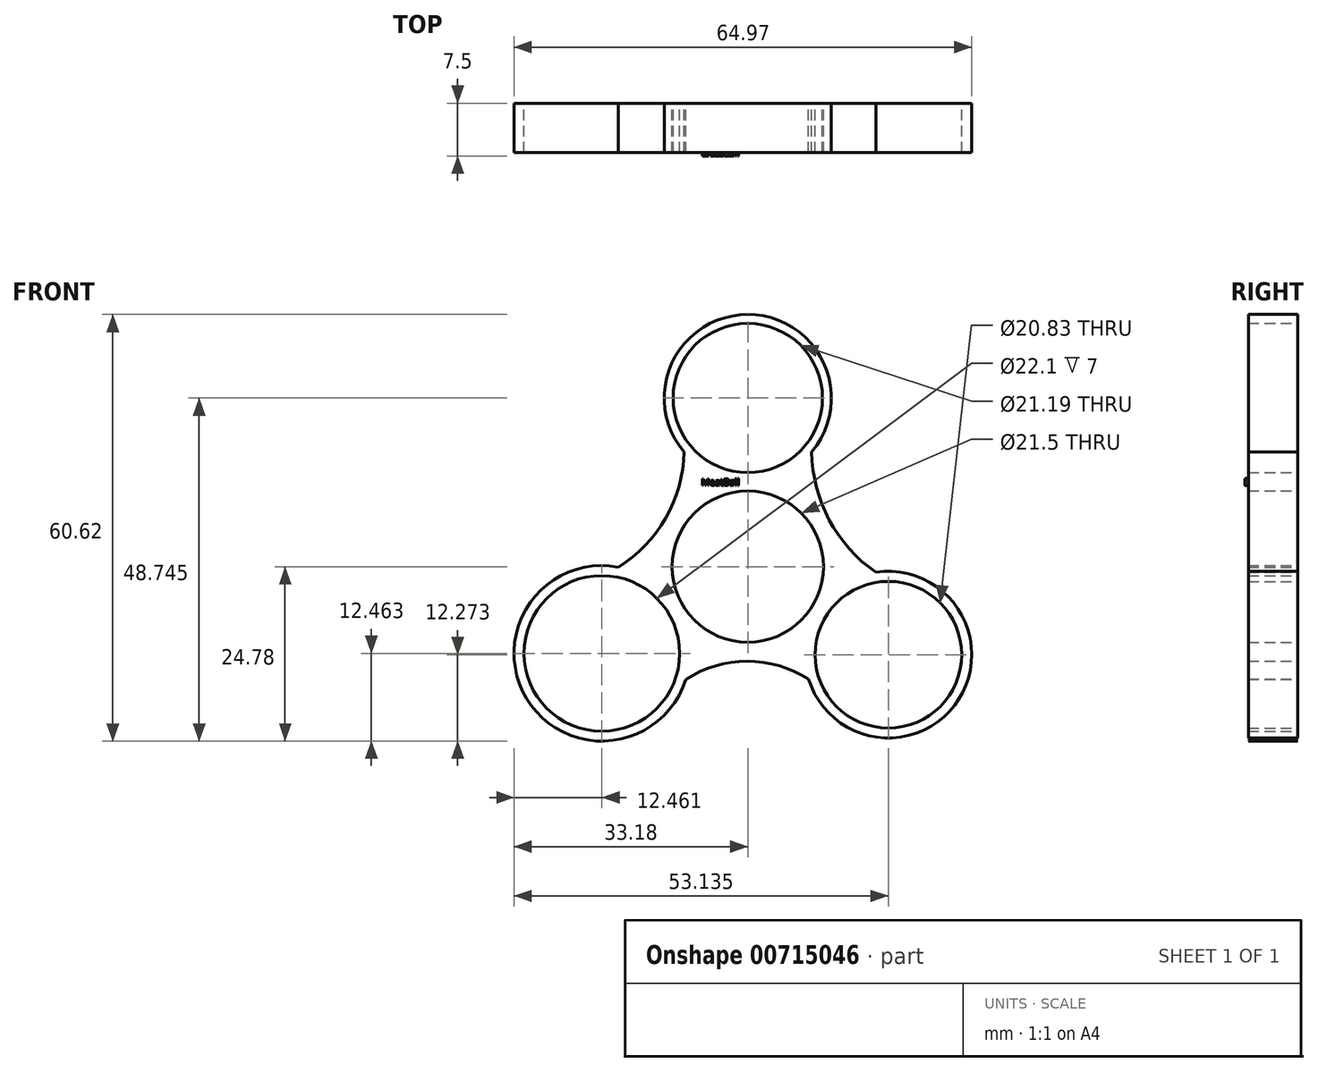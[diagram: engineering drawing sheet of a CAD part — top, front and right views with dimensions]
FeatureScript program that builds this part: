
annotation { "Feature Type Name" : "Feature", "Feature Type Description" : "" }
export const myFeature = defineFeature(function(context is Context, id is Id, definition is map)
    precondition{}
    {
        {
            var Q0;
            Q0=qCreatedBy(makeId("Front.planeOp"),FACE);
            var sketch = newSketch(context, id + "F0", { "sketchPlane" : qUnion([Q0])});
            skCircle(sketch, "E0", {"center": v(0, 23.96) * mm, "radius": 10.6 * mm});
            skCircle(sketch, "E1", {"center": v(0, 0) * mm, "radius": 10.75 * mm});
            skCircle(sketch, "E2", {"center": v(-20.72, -12.32) * mm, "radius": 11.05 * mm});
            skCircle(sketch, "E3", {"center": v(19.95, -12.5) * mm, "radius": 10.41 * mm});
            skLineSegment(sketch, "E4", {"start": v(0, 23.96) * mm, "end": v(0, 40.58) * mm});
            skLineSegment(sketch, "E5", {"start": v(0, 23.96) * mm, "end": v(14.66, 15.5) * mm});
            skLineSegment(sketch, "E6", {"start": v(0, 23.96) * mm, "end": v(-14.66, 15.5) * mm});
            skLineSegment(sketch, "E7", {"start": v(-20.72, -12.32) * mm, "end": v(-20.72, 8.12) * mm});
            skLineSegment(sketch, "E8", {"start": v(-20.72, -10.79) * mm, "end": v(-20.72, -14.42) * mm});
            skLineSegment(sketch, "E9", {"start": v(-20.72, -12.32) * mm, "end": v(-42.47, -24.87) * mm});
            skLineSegment(sketch, "E10", {"start": v(-20.72, -12.32) * mm, "end": v(-2.62, -22.76) * mm});
            skLineSegment(sketch, "E11", {"start": v(19.95, -12.5) * mm, "end": v(19.95, 8.69) * mm});
            skLineSegment(sketch, "E12", {"start": v(19.95, -12.5) * mm, "end": v(35.57, -21.52) * mm});
            skLineSegment(sketch, "E13", {"start": v(19.95, -12.5) * mm, "end": v(2.82, -22.4) * mm});
            skArc(sketch, "E14", {"start": v(9.18, 18.67) * mm, "mid": v(11.5, 6.77) * mm, "end": v(19.95, -1.9) * mm});
            skArc(sketch, "E15", {"start": v(-20.72, -1.27) * mm, "mid": v(-11.68, 6.81) * mm, "end": v(-9.18, 18.67) * mm});
            skArc(sketch, "E16", {"start": v(10.94, -17.71) * mm, "mid": v(-0.13, -13.45) * mm, "end": v(-11.15, -17.84) * mm});
            skCircle(sketch, "E17", {"center": v(0, 23.96) * mm, "radius": 11.87 * mm});
            skCircle(sketch, "E18", {"center": v(-20.72, -12.32) * mm, "radius": 12.46 * mm});
            skCircle(sketch, "E19", {"center": v(19.95, -12.5) * mm, "radius": 11.84 * mm});
            skSolve(sketch);
        }
        {
            var Q0;
            Q0 = qSketchRegion(id + "F0", true);
            extrude(context, id + "F1", {"entities" : qUnion([Q0]), "depth" : 7 * mm, "offsetDistance" : 25.4 * mm});
        }
        {
            var Q0;
            Q0=makeQuery(id+"F1.opExtrude","CAP_FACE",FACE,{"disambiguationData":[OSD([sQuery(id+"F0.wireOp",EDGE,"E0"),sQuery(id+"F0.wireOp",EDGE,"E1"),sQuery(id+"F0.wireOp",EDGE,"E2"),sQuery(id+"F0.wireOp",EDGE,"E3"),sQuery(id+"F0.wireOp",EDGE,"E14"),sQuery(id+"F0.wireOp",EDGE,"E15"),sQuery(id+"F0.wireOp",EDGE,"E16"),sQuery(id+"F0.wireOp",EDGE,"E17"),sQuery(id+"F0.wireOp",EDGE,"E18"),sQuery(id+"F0.wireOp",EDGE,"E19")])],"isStart":false});
            var sketch = newSketch(context, id + "F2", { "sketchPlane" : qUnion([Q0])});
            skText(sketch, "E20", { "text": "MeatBall\n", "fontName": "OpenSans-Regular.ttf"});
            const initialGuessF2  = {"E20": [-0.00659, 0.01155, 1, 0, 0.00095]};
            skSetInitialGuess(sketch, initialGuessF2);
            skSolve(sketch);
        }
        {
            var Q0;
            Q0 = qSketchRegion(id + "F2", true);
            extrude(context, id + "F3", {"entities" : qUnion([Q0]), "operationType" : NewBodyOperationType.ADD, "depth" : .5 * mm, "offsetDistance" : 25.4 * mm});
        }
    });
